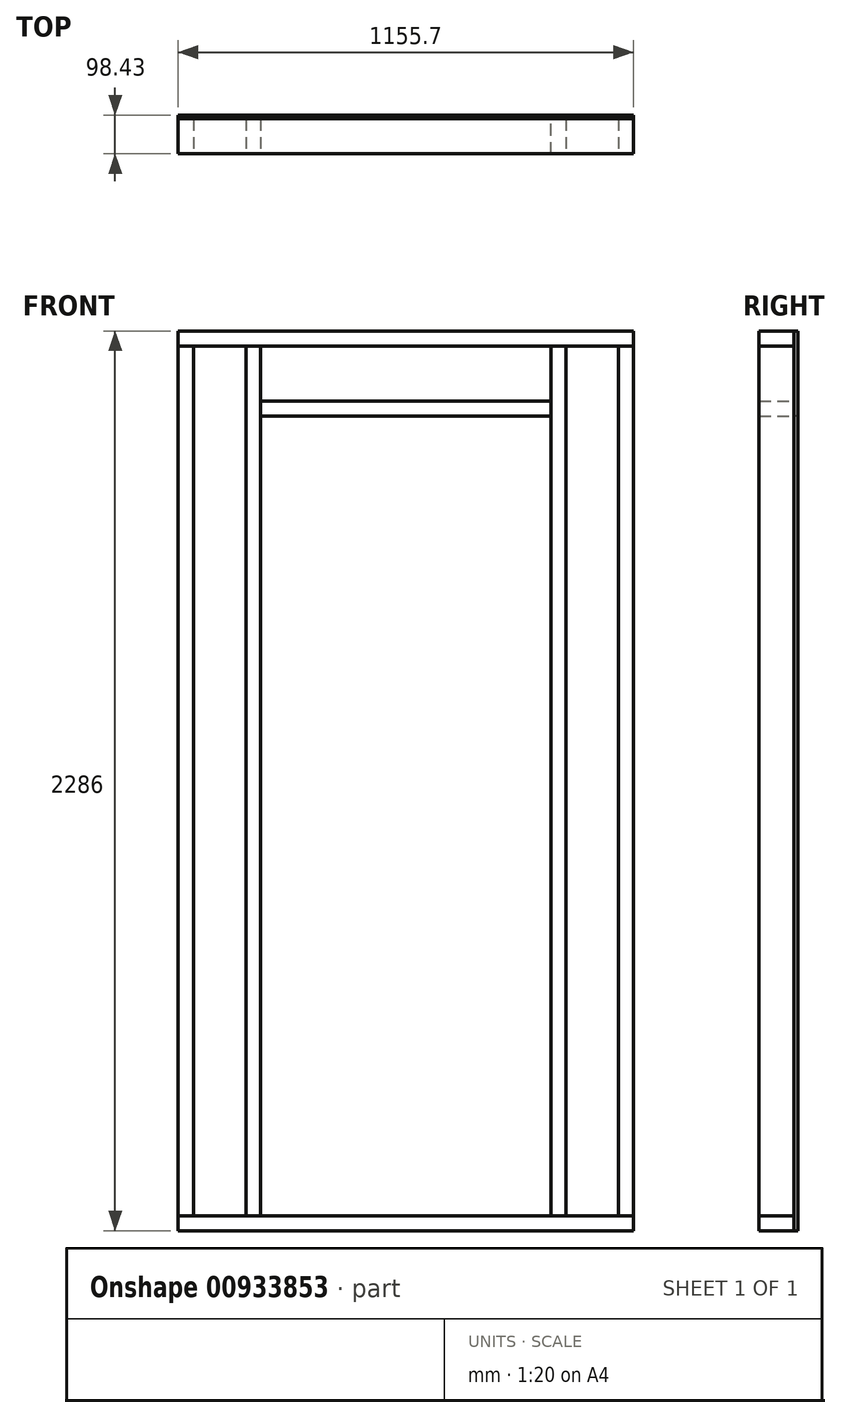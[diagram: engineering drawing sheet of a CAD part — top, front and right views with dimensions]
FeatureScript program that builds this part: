
annotation { "Feature Type Name" : "Feature", "Feature Type Description" : "" }
export const myFeature = defineFeature(function(context is Context, id is Id, definition is map)
    precondition{}
    {
        {
            var Q0;
            Q0=qCreatedBy(makeId("Top.planeOp"),FACE);
            var sketch = newSketch(context, id + "F0", { "sketchPlane" : qUnion([Q0])});
            skLineSegment(sketch, "E0.bottom", {"start": v(0, 0) * mm, "end": v(1155.7, 0) * mm});
            skLineSegment(sketch, "E0.top", {"start": v(0, -88.9) * mm, "end": v(1155.7, -88.9) * mm});
            skLineSegment(sketch, "E0.left", {"start": v(0, 0) * mm, "end": v(0, -88.9) * mm});
            skLineSegment(sketch, "E0.right", {"start": v(1155.7, 0) * mm, "end": v(1155.7, -88.9) * mm});
            skSolve(sketch);
        }
        {
            var Q0;
            Q0 = qSketchRegion(id + "F0", true);
            extrude(context, id + "F1", {"entities" : qUnion([Q0]), "depth" : 38.1 * mm, "offsetDistance" : 25.4 * mm});
        }
        {
            var Q0;
            Q0=makeQuery(id+"F1.opExtrude","CAP_FACE",FACE,{"disambiguationData":[OSD([sQuery(id+"F0.wireOp",EDGE,"E0.bottom"),sQuery(id+"F0.wireOp",EDGE,"E0.top"),sQuery(id+"F0.wireOp",EDGE,"E0.left"),sQuery(id+"F0.wireOp",EDGE,"E0.right")])],"isStart":false});
            var sketch = newSketch(context, id + "F2", { "sketchPlane" : qUnion([Q0])});
            skLineSegment(sketch, "E1.bottom", {"start": v(0, 0) * mm, "end": v(38.1, 0) * mm});
            skLineSegment(sketch, "E1.top", {"start": v(0, -88.9) * mm, "end": v(38.1, -88.9) * mm});
            skLineSegment(sketch, "E1.left", {"start": v(0, 0) * mm, "end": v(0, -88.9) * mm});
            skLineSegment(sketch, "E1.right", {"start": v(38.1, 0) * mm, "end": v(38.1, -88.9) * mm});
            skLineSegment(sketch, "E2.bottom", {"start": v(1155.7, 0) * mm, "end": v(1117.6, 0) * mm});
            skLineSegment(sketch, "E2.top", {"start": v(1155.7, -88.9) * mm, "end": v(1117.6, -88.9) * mm});
            skLineSegment(sketch, "E2.left", {"start": v(1155.7, 0) * mm, "end": v(1155.7, -88.9) * mm});
            skLineSegment(sketch, "E2.right", {"start": v(1117.6, 0) * mm, "end": v(1117.6, -88.9) * mm});
            skLineSegment(sketch, "E3.bottom", {"start": v(171.45, 0) * mm, "end": v(209.55, 0) * mm});
            skLineSegment(sketch, "E3.top", {"start": v(171.45, -88.9) * mm, "end": v(209.55, -88.9) * mm});
            skLineSegment(sketch, "E3.left", {"start": v(171.45, 0) * mm, "end": v(171.45, -88.9) * mm});
            skLineSegment(sketch, "E3.right", {"start": v(209.55, 0) * mm, "end": v(209.55, -88.9) * mm});
            skLineSegment(sketch, "E4.bottom", {"start": v(946.15, 0) * mm, "end": v(984.25, 0) * mm});
            skLineSegment(sketch, "E4.top", {"start": v(946.15, -88.9) * mm, "end": v(984.25, -88.9) * mm});
            skLineSegment(sketch, "E4.left", {"start": v(946.15, 0) * mm, "end": v(946.15, -88.9) * mm});
            skLineSegment(sketch, "E4.right", {"start": v(984.25, 0) * mm, "end": v(984.25, -88.9) * mm});
            skSolve(sketch);
        }
        {
            var Q0;
            Q0 = qSketchRegion(id + "F2", true);
            extrude(context, id + "F3", {"entities" : qUnion([Q0]), "depth" : 2209.8 * mm, "offsetDistance" : 25.4 * mm});
        }
        {
            var Q0;
            Q0=makeQuery(id+"F3.opExtrude","CAP_FACE",FACE,{"disambiguationData":[OSD([sQuery(id+"F2.wireOp",EDGE,"E2.bottom"),sQuery(id+"F2.wireOp",EDGE,"E2.top"),sQuery(id+"F2.wireOp",EDGE,"E2.left"),sQuery(id+"F2.wireOp",EDGE,"E2.right")])],"isStart":false});
            var sketch = newSketch(context, id + "F4", { "sketchPlane" : qUnion([Q0])});
            skLineSegment(sketch, "E5.bottom", {"start": v(1155.7, -88.9) * mm, "end": v(0, -88.9) * mm});
            skLineSegment(sketch, "E5.top", {"start": v(1155.7, 0) * mm, "end": v(0, 0) * mm});
            skLineSegment(sketch, "E5.left", {"start": v(1155.7, -88.9) * mm, "end": v(1155.7, 0) * mm});
            skLineSegment(sketch, "E5.right", {"start": v(0, -88.9) * mm, "end": v(0, 0) * mm});
            skSolve(sketch);
        }
        {
            var Q0;
            Q0 = qSketchRegion(id + "F4", true);
            extrude(context, id + "F5", {"entities" : qUnion([Q0]), "depth" : 38.1 * mm, "offsetDistance" : 25.4 * mm});
        }
        {
            var Q0;
            Q0=makeQuery(id+"F3.opExtrude","SWEPT_FACE",FACE,{"disambiguationData":[OSD([sQuery(id+"F2.wireOp",EDGE,"E3.right")])]});
            var sketch = newSketch(context, id + "F6", { "sketchPlane" : qUnion([Q0])});
            skLineSegment(sketch, "E6.bottom", {"start": v(-88.9, 2108.2) * mm, "end": v(0, 2108.2) * mm});
            skLineSegment(sketch, "E6.top", {"start": v(-88.9, 2070.1) * mm, "end": v(0, 2070.1) * mm});
            skLineSegment(sketch, "E6.left", {"start": v(-88.9, 2108.2) * mm, "end": v(-88.9, 2070.1) * mm});
            skLineSegment(sketch, "E6.right", {"start": v(0, 2108.2) * mm, "end": v(0, 2070.1) * mm});
            skSolve(sketch);
        }
        {
            var Q0;
            Q0 = qSketchRegion(id + "F6", true);
            extrude(context, id + "F7", {"entities" : qUnion([Q0]), "depth" : 736.6 * mm, "offsetDistance" : 25.4 * mm});
        }
        {
            var Q0;
            Q0=makeQuery(id+"F5.opExtrude","SWEPT_FACE",FACE,{"disambiguationData":[OSD([sQuery(id+"F4.wireOp",EDGE,"E5.top")])]});
            var sketch = newSketch(context, id + "F8", { "sketchPlane" : qUnion([Q0])});
            skLineSegment(sketch, "E7.bottom", {"start": v(-1155.7, 2286) * mm, "end": v(-946.15, 2286) * mm});
            skLineSegment(sketch, "E7.top", {"start": v(-1155.7, 0) * mm, "end": v(-946.15, 0) * mm});
            skLineSegment(sketch, "E7.left", {"start": v(-1155.7, 2286) * mm, "end": v(-1155.7, 0) * mm});
            skLineSegment(sketch, "E7.right", {"start": v(-946.15, 2286) * mm, "end": v(-946.15, 0) * mm});
            skLineSegment(sketch, "E8.bottom", {"start": v(0, 0) * mm, "end": v(-209.55, 0) * mm});
            skLineSegment(sketch, "E8.top", {"start": v(0, 2286) * mm, "end": v(-209.55, 2286) * mm});
            skLineSegment(sketch, "E8.left", {"start": v(0, 0) * mm, "end": v(0, 2286) * mm});
            skLineSegment(sketch, "E8.right", {"start": v(-209.55, 0) * mm, "end": v(-209.55, 2286) * mm});
            skSolve(sketch);
        }
        {
            var Q0;
            Q0 = qSketchRegion(id + "F8", true);
            extrude(context, id + "F9", {"entities" : qUnion([Q0]), "depth" : 9.52 * mm, "offsetDistance" : 25.4 * mm});
        }
        {
            var Q0;
            Q0=makeQuery(id+"F5.opExtrude","SWEPT_FACE",FACE,{"disambiguationData":[OSD([sQuery(id+"F4.wireOp",EDGE,"E5.top")])]});
            var sketch = newSketch(context, id + "F10", { "sketchPlane" : qUnion([Q0])});
            skLineSegment(sketch, "E9.bottom", {"start": v(-946.15, 2286) * mm, "end": v(-209.55, 2286) * mm});
            skLineSegment(sketch, "E9.top", {"start": v(-946.15, 2070.1) * mm, "end": v(-209.55, 2070.1) * mm});
            skLineSegment(sketch, "E9.left", {"start": v(-946.15, 2286) * mm, "end": v(-946.15, 2070.1) * mm});
            skLineSegment(sketch, "E9.right", {"start": v(-209.55, 2286) * mm, "end": v(-209.55, 2070.1) * mm});
            skSolve(sketch);
        }
        {
            var Q0;
            Q0 = qSketchRegion(id + "F10", true);
            extrude(context, id + "F11", {"entities" : qUnion([Q0]), "depth" : 9.52 * mm, "offsetDistance" : 25.4 * mm});
        }
    });
